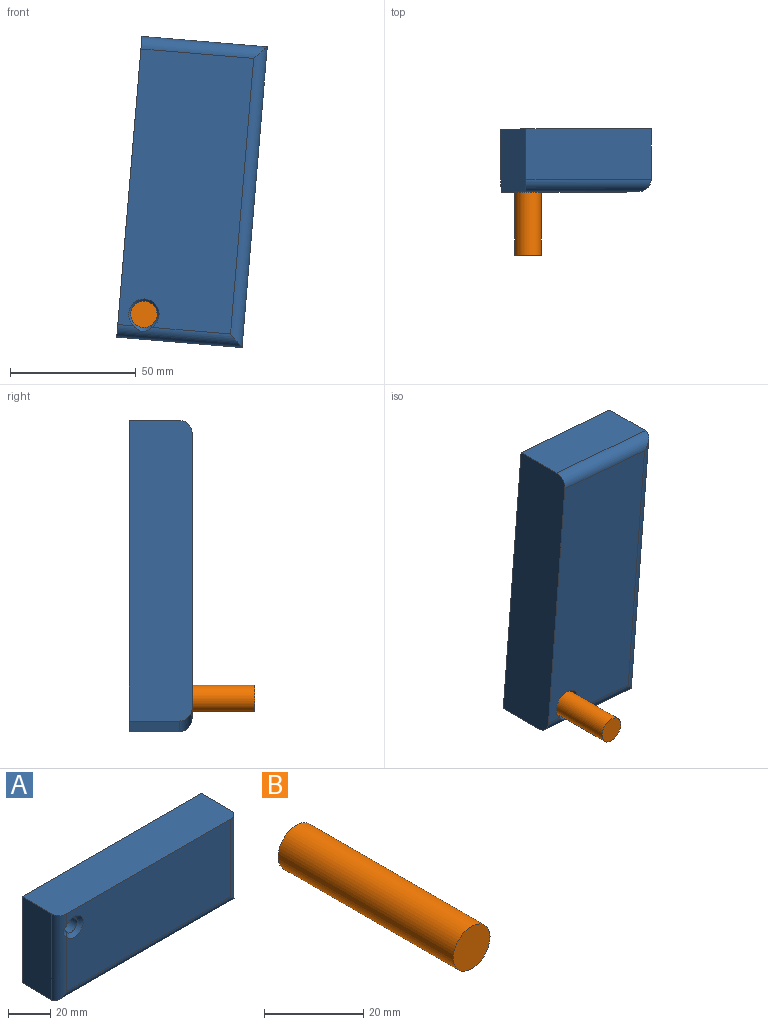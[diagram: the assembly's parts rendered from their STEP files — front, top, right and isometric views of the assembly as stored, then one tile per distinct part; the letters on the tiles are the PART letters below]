
ASSEMBLY  parts=2 mates=1
PART A: 12 faces, bbox 120x25x50 mm
  f0: plane 50x20mm, normal (-1,0,0), area 1000mm2, adj f1,f4,f6,f7
  f1: plane 120x20mm, normal (0,0,-1), area 2400mm2, adj f0,f2,f6,f8
  f2: plane 50x20mm, normal (1,0,0), area 1000mm2, adj f1,f4,f6,f9
  f3: cylinder r=4.09mm len=23mm, axis (0,1,0), area 591.7mm2, adj f6,f10,f11
  f4: plane 120x25mm, normal (0,0,1), area 2989.3mm2, adj f0,f2,f5,f6,f7,f9
  f5: plane 110x45mm, normal (0,-1,0), area 4838.9mm2, adj f4,f7,f8,f9,f10
  f6: plane 120x50mm, normal (0,1,0), area 5947.3mm2, adj f0,f1,f2,f3,f4
  f7: cylinder r=5mm len=50mm, axis (0,0,1), area 363.6mm2, adj f0,f4,f5,f8,f11
  f8: cylinder r=5mm len=120mm, axis (-1,0,0), area 903.2mm2, adj f1,f5,f7,f9
  f9: cylinder r=5mm len=50mm, axis (0,0,-1), area 373.1mm2, adj f2,f4,f5,f8
  f10: cone r=4.09mm half-angle=45deg, axis (0,-1,0), area 72.6mm2, adj f3,f5,f11
  f11: bspline ~7.12x3.54mm, area 21.1mm2, adj f3,f7,f10
PART B: 3 faces, bbox 10.5x50x10.5 mm
  f0: cylinder r=5.25mm len=50mm, axis (0,1,0), area 1648mm2, adj f1,f2
  f1: plane 10.49x10.49mm, normal (0,-1,0), area 86.4mm2, adj f0
  f2: plane 10.49x10.49mm, normal (0,1,0), area 86.4mm2, adj f0
PLACE A rot(axis=(0,-1,0),85.2deg) t=(8.07,22.03,-79.54)mm
PLACE B t=(78.43,22.03,-128.53)mm fixed
MATE revolute B.f0 <-> A.f3  axis (0,1,0) through (18.86,22.03,-70.47)mm
